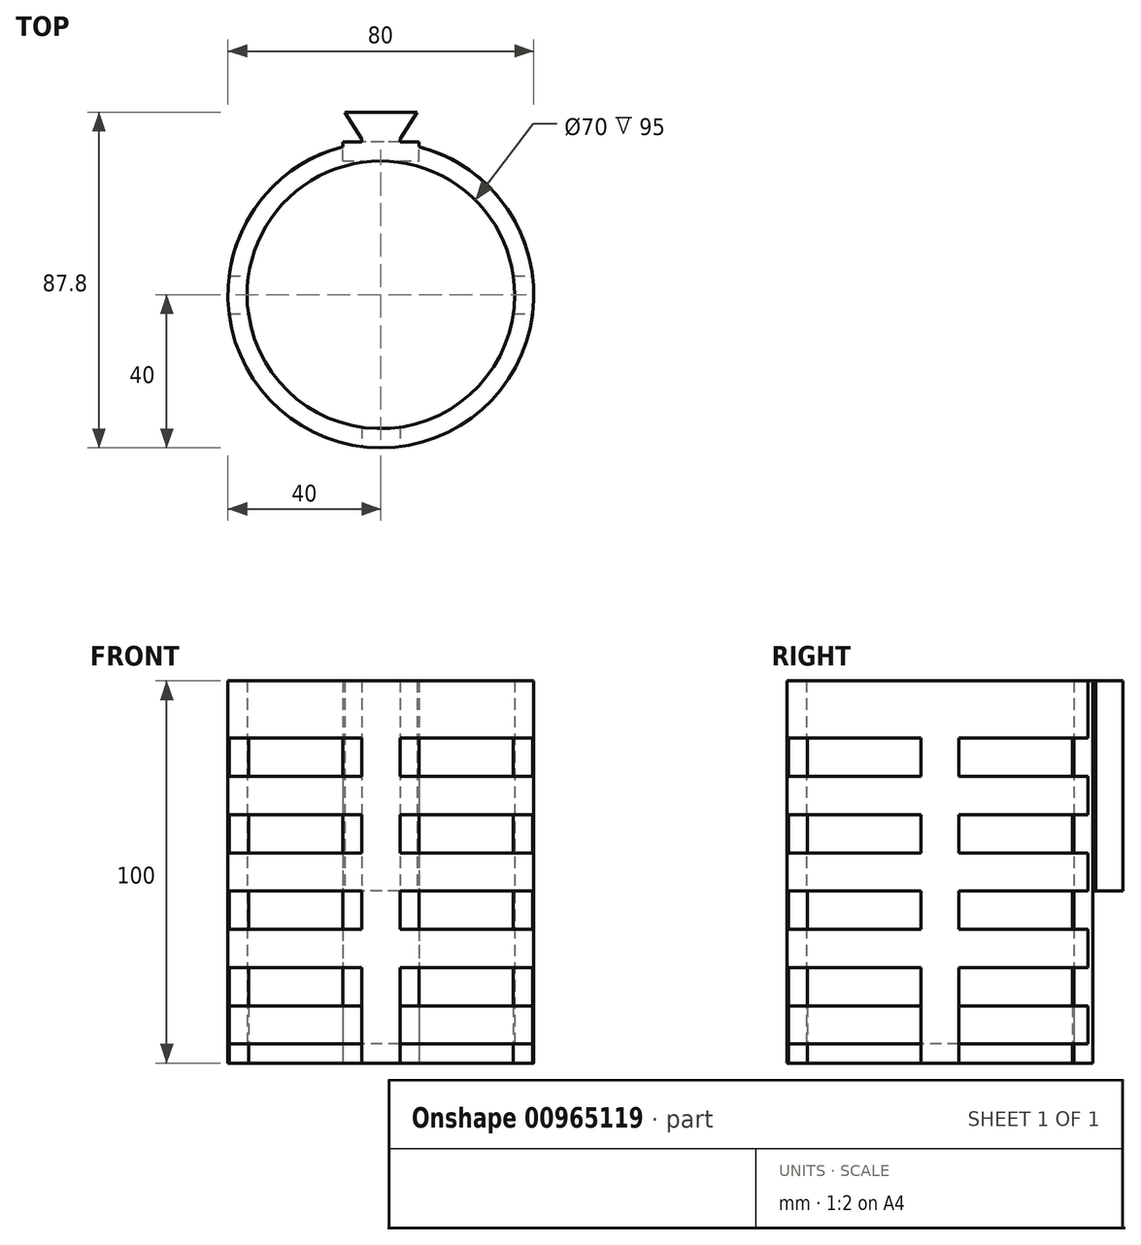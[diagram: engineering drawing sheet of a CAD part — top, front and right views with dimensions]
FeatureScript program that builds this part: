
annotation { "Feature Type Name" : "Feature", "Feature Type Description" : "" }
export const myFeature = defineFeature(function(context is Context, id is Id, definition is map)
    precondition{}
    {
        {
            var Q0;
            Q0=qCreatedBy(makeId("Top.planeOp"),FACE);
            var sketch = newSketch(context, id + "F0", { "sketchPlane" : qUnion([Q0])});
            skCircle(sketch, "E0", {"center": v(0, 0) * mm, "radius": 35 * mm});
            skArc(sketch, "E1", {"start": v(-10, 38.73) * mm, "mid": v(0, -40) * mm, "end": v(10, 38.73) * mm});
            skLineSegment(sketch, "E2", {"start": v(5, 34.64) * mm, "end": v(5, 35) * mm});
            skLineSegment(sketch, "E3", {"start": v(-5, 34.64) * mm, "end": v(-5, 35) * mm});
            skLineSegment(sketch, "E4", {"start": v(-5, -34.64) * mm, "end": v(-5, -39.69) * mm});
            skLineSegment(sketch, "E5", {"start": v(5, -34.64) * mm, "end": v(5, -39.69) * mm});
            skLineSegment(sketch, "E6", {"start": v(-39.69, 5) * mm, "end": v(-34.64, 5) * mm});
            skLineSegment(sketch, "E7", {"start": v(-39.69, -5) * mm, "end": v(-34.64, -5) * mm});
            skLineSegment(sketch, "E8", {"start": v(34.64, 5) * mm, "end": v(39.69, 5) * mm});
            skLineSegment(sketch, "E9", {"start": v(34.64, -5) * mm, "end": v(39.69, -5) * mm});
            skLineSegment(sketch, "E10", {"start": v(-10, 35) * mm, "end": v(-5, 35) * mm});
            skLineSegment(sketch, "E11", {"start": v(10, 35) * mm, "end": v(10, 40) * mm});
            skLineSegment(sketch, "E12", {"start": v(10, 40) * mm, "end": v(-10, 40) * mm});
            skLineSegment(sketch, "E13", {"start": v(-10, 35) * mm, "end": v(-10, 40) * mm});
            skLineSegment(sketch, "E14", {"start": v(-5, 40) * mm, "end": v(-5, 40.8) * mm});
            skLineSegment(sketch, "E15", {"start": v(5, 40.8) * mm, "end": v(5, 40) * mm});
            skLineSegment(sketch, "E16", {"start": v(5, 40.8) * mm, "end": v(9.5, 47.8) * mm});
            skLineSegment(sketch, "E17", {"start": v(9.5, 47.8) * mm, "end": v(-9.5, 47.8) * mm});
            skLineSegment(sketch, "E18", {"start": v(-9.5, 47.8) * mm, "end": v(-5, 40.8) * mm});
            skPoint(sketch, "E19.orphan", {"position": v(5, 39.69) * mm});
            skPoint(sketch, "E20.orphan", {"position": v(-5, 39.69) * mm});
            skLineSegment(sketch, "E21.trimOffspring", {"start": v(5, 35) * mm, "end": v(10, 35) * mm});
            skSolve(sketch);
        }
        {
            var Q0;
            {var subQ0=sQuery(id+"F0.wireOp",EDGE,"E0");var subQ4=makeQuery(id+"F0.imprint","INTERSECT",VERTEX,{"derivedFrom":[subQ0,sQuery(id+"F0.wireOp",EDGE,"E2")]});Q0=makeQuery(id+"F0.imprint","IMPRINT",FACE,{"disambiguationData":[TD([[makeQuery(id+"F0.imprint","IMPRINT",EDGE,{"disambiguationData":[TD([[subQ4,1.0]])],"derivedFrom":subQ0}),1.0]])]});}
            extrude(context, id + "F1", {"entities" : qUnion([Q0]), "depth" : 5 * mm, "offsetDistance" : 25 * mm});
        }
        {
            var Q0;
            {var subQ0=sQuery(id+"F0.wireOp",EDGE,"E6");Q0=makeQuery(id+"F0.imprint","IMPRINT",FACE,{"disambiguationData":[TD([[makeQuery(id+"F0.imprint","IMPRINT",EDGE,{"derivedFrom":subQ0}),-1.0]])]});}
            var Q1;
            {var subQ0=sQuery(id+"F0.wireOp",EDGE,"E4");Q1=makeQuery(id+"F0.imprint","IMPRINT",FACE,{"disambiguationData":[TD([[makeQuery(id+"F0.imprint","IMPRINT",EDGE,{"derivedFrom":subQ0}),1.0]])]});}
            var Q2;
            {var subQ0=sQuery(id+"F0.wireOp",EDGE,"E8");Q2=makeQuery(id+"F0.imprint","IMPRINT",FACE,{"disambiguationData":[TD([[makeQuery(id+"F0.imprint","IMPRINT",EDGE,{"derivedFrom":subQ0}),-1.0]])]});}
            var Q3;
            {var subQ11=sQuery(id+"F0.wireOp",EDGE,"E2");Q3=makeQuery(id+"F0.imprint","IMPRINT",FACE,{"disambiguationData":[TD([[makeQuery(id+"F0.imprint","IMPRINT",EDGE,{"derivedFrom":subQ11}),1.0]])]});}
            extrude(context, id + "F2", {"entities" : qUnion([Q0, Q1, Q2, Q3]), "operationType" : NewBodyOperationType.ADD, "depth" : 100 * mm, "offsetDistance" : 25 * mm});
        }
        {
            var Q0;
            {var subQ0=sQuery(id+"F0.wireOp",EDGE,"E4");Q0=makeQuery(id+"F0.imprint","IMPRINT",FACE,{"disambiguationData":[TD([[makeQuery(id+"F0.imprint","IMPRINT",EDGE,{"derivedFrom":subQ0}),-1.0]])]});}
            var Q1;
            {var subQ0=sQuery(id+"F0.wireOp",EDGE,"E5");Q1=makeQuery(id+"F0.imprint","IMPRINT",FACE,{"disambiguationData":[TD([[makeQuery(id+"F0.imprint","IMPRINT",EDGE,{"derivedFrom":subQ0}),1.0]])]});}
            var Q2;
            {var subQ5=sQuery(id+"F0.wireOp",EDGE,"E2");Q2=makeQuery(id+"F0.imprint","IMPRINT",FACE,{"disambiguationData":[TD([[makeQuery(id+"F0.imprint","IMPRINT",EDGE,{"derivedFrom":subQ5}),-1.0]])]});}
            var Q3;
            {var subQ4=sQuery(id+"F0.wireOp",EDGE,"E3");Q3=makeQuery(id+"F0.imprint","IMPRINT",FACE,{"disambiguationData":[TD([[makeQuery(id+"F0.imprint","IMPRINT",EDGE,{"derivedFrom":subQ4}),1.0]])]});}
            extrude(context, id + "F3", {"entities" : qUnion([Q0, Q1, Q2, Q3]), "depth" : 15 * mm, "offsetDistance" : 25 * mm, "hasSecondDirection" : true, "secondDirectionOppositeDirection" : false, "secondDirectionDepth" : 5 * mm});
        }
        {
            var Q0;
            {var subQ0=sQuery(id+"F0.wireOp",EDGE,"E4");Q0=makeQuery(id+"F0.imprint","IMPRINT",FACE,{"disambiguationData":[TD([[makeQuery(id+"F0.imprint","IMPRINT",EDGE,{"derivedFrom":subQ0}),-1.0]])]});}
            var Q1;
            {var subQ4=sQuery(id+"F0.wireOp",EDGE,"E3");Q1=makeQuery(id+"F0.imprint","IMPRINT",FACE,{"disambiguationData":[TD([[makeQuery(id+"F0.imprint","IMPRINT",EDGE,{"derivedFrom":subQ4}),1.0]])]});}
            var Q2;
            {var subQ5=sQuery(id+"F0.wireOp",EDGE,"E2");Q2=makeQuery(id+"F0.imprint","IMPRINT",FACE,{"disambiguationData":[TD([[makeQuery(id+"F0.imprint","IMPRINT",EDGE,{"derivedFrom":subQ5}),-1.0]])]});}
            var Q3;
            {var subQ0=sQuery(id+"F0.wireOp",EDGE,"E5");Q3=makeQuery(id+"F0.imprint","IMPRINT",FACE,{"disambiguationData":[TD([[makeQuery(id+"F0.imprint","IMPRINT",EDGE,{"derivedFrom":subQ0}),1.0]])]});}
            extrude(context, id + "F4", {"entities" : qUnion([Q0, Q1, Q2, Q3]), "operationType" : NewBodyOperationType.ADD, "depth" : 35 * mm, "offsetDistance" : 25 * mm, "hasSecondDirection" : true, "secondDirectionOppositeDirection" : false, "secondDirectionDepth" : 25 * mm});
        }
        {
            var Q0;
            {var subQ0=sQuery(id+"F0.wireOp",EDGE,"E14");Q0=makeQuery(id+"F0.imprint","IMPRINT",FACE,{"disambiguationData":[TD([[makeQuery(id+"F0.imprint","IMPRINT",EDGE,{"derivedFrom":subQ0}),-1.0]])]});}
            extrude(context, id + "F5", {"entities" : qUnion([Q0]), "operationType" : NewBodyOperationType.ADD, "depth" : 100 * mm, "offsetDistance" : 25 * mm, "hasSecondDirection" : true, "secondDirectionOppositeDirection" : false, "secondDirectionDepth" : 45 * mm});
        }
        {
            var Q0;
            {var subQ4=sQuery(id+"F0.wireOp",EDGE,"E3");Q0=makeQuery(id+"F0.imprint","IMPRINT",FACE,{"disambiguationData":[TD([[makeQuery(id+"F0.imprint","IMPRINT",EDGE,{"derivedFrom":subQ4}),1.0]])]});}
            var Q1;
            {var subQ0=sQuery(id+"F0.wireOp",EDGE,"E4");Q1=makeQuery(id+"F0.imprint","IMPRINT",FACE,{"disambiguationData":[TD([[makeQuery(id+"F0.imprint","IMPRINT",EDGE,{"derivedFrom":subQ0}),-1.0]])]});}
            var Q2;
            {var subQ0=sQuery(id+"F0.wireOp",EDGE,"E5");Q2=makeQuery(id+"F0.imprint","IMPRINT",FACE,{"disambiguationData":[TD([[makeQuery(id+"F0.imprint","IMPRINT",EDGE,{"derivedFrom":subQ0}),1.0]])]});}
            var Q3;
            {var subQ5=sQuery(id+"F0.wireOp",EDGE,"E2");Q3=makeQuery(id+"F0.imprint","IMPRINT",FACE,{"disambiguationData":[TD([[makeQuery(id+"F0.imprint","IMPRINT",EDGE,{"derivedFrom":subQ5}),-1.0]])]});}
            extrude(context, id + "F6", {"entities" : qUnion([Q0, Q1, Q2, Q3]), "operationType" : NewBodyOperationType.ADD, "depth" : 55 * mm, "offsetDistance" : 25 * mm, "hasSecondDirection" : true, "secondDirectionOppositeDirection" : false, "secondDirectionDepth" : 45 * mm});
        }
        {
            var Q0;
            {var subQ0=sQuery(id+"F0.wireOp",EDGE,"E5");Q0=makeQuery(id+"F0.imprint","IMPRINT",FACE,{"disambiguationData":[TD([[makeQuery(id+"F0.imprint","IMPRINT",EDGE,{"derivedFrom":subQ0}),1.0]])]});}
            var Q1;
            {var subQ0=sQuery(id+"F0.wireOp",EDGE,"E4");Q1=makeQuery(id+"F0.imprint","IMPRINT",FACE,{"disambiguationData":[TD([[makeQuery(id+"F0.imprint","IMPRINT",EDGE,{"derivedFrom":subQ0}),-1.0]])]});}
            var Q2;
            {var subQ4=sQuery(id+"F0.wireOp",EDGE,"E3");Q2=makeQuery(id+"F0.imprint","IMPRINT",FACE,{"disambiguationData":[TD([[makeQuery(id+"F0.imprint","IMPRINT",EDGE,{"derivedFrom":subQ4}),1.0]])]});}
            var Q3;
            {var subQ5=sQuery(id+"F0.wireOp",EDGE,"E2");Q3=makeQuery(id+"F0.imprint","IMPRINT",FACE,{"disambiguationData":[TD([[makeQuery(id+"F0.imprint","IMPRINT",EDGE,{"derivedFrom":subQ5}),-1.0]])]});}
            extrude(context, id + "F7", {"entities" : qUnion([Q0, Q1, Q2, Q3]), "operationType" : NewBodyOperationType.ADD, "depth" : 75 * mm, "offsetDistance" : 25 * mm, "hasSecondDirection" : true, "secondDirectionOppositeDirection" : false, "secondDirectionDepth" : 65 * mm});
        }
        {
            var Q0;
            {var subQ0=sQuery(id+"F0.wireOp",EDGE,"E5");Q0=makeQuery(id+"F0.imprint","IMPRINT",FACE,{"disambiguationData":[TD([[makeQuery(id+"F0.imprint","IMPRINT",EDGE,{"derivedFrom":subQ0}),1.0]])]});}
            var Q1;
            {var subQ0=sQuery(id+"F0.wireOp",EDGE,"E4");Q1=makeQuery(id+"F0.imprint","IMPRINT",FACE,{"disambiguationData":[TD([[makeQuery(id+"F0.imprint","IMPRINT",EDGE,{"derivedFrom":subQ0}),-1.0]])]});}
            var Q2;
            {var subQ4=sQuery(id+"F0.wireOp",EDGE,"E3");Q2=makeQuery(id+"F0.imprint","IMPRINT",FACE,{"disambiguationData":[TD([[makeQuery(id+"F0.imprint","IMPRINT",EDGE,{"derivedFrom":subQ4}),1.0]])]});}
            var Q3;
            {var subQ5=sQuery(id+"F0.wireOp",EDGE,"E2");Q3=makeQuery(id+"F0.imprint","IMPRINT",FACE,{"disambiguationData":[TD([[makeQuery(id+"F0.imprint","IMPRINT",EDGE,{"derivedFrom":subQ5}),-1.0]])]});}
            extrude(context, id + "F8", {"entities" : qUnion([Q0, Q1, Q2, Q3]), "operationType" : NewBodyOperationType.ADD, "depth" : 100 * mm, "offsetDistance" : 25 * mm, "hasSecondDirection" : true, "secondDirectionOppositeDirection" : false, "secondDirectionDepth" : 85 * mm});
        }
    });
